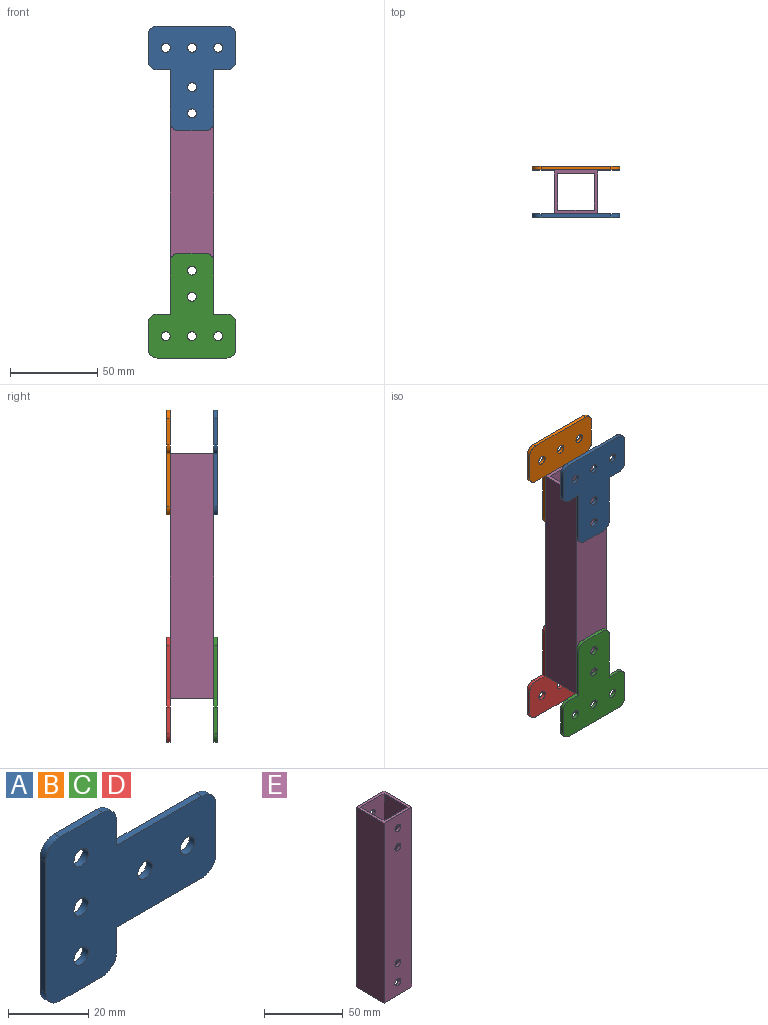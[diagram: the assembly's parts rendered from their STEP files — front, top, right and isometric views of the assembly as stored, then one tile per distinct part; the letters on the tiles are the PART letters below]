
ASSEMBLY  parts=5 mates=4
PART A: 21 faces, bbox 60x2x50 mm
  f0: plane 7.5x2mm, normal (1,0,0), area 15mm2, adj f12,f13,f14,f15
  f1: plane 15x2mm, normal (0,0,1), area 30mm2, adj f13,f14,f15,f16
  f2: plane 40x2mm, normal (-1,0,0), area 80mm2, adj f13,f14,f16,f17
  f3: plane 15x2mm, normal (0,0,-1), area 30mm2, adj f13,f14,f17,f18
  f4: plane 7.5x2mm, normal (1,0,0), area 15mm2, adj f5,f13,f14,f18
  f5: plane 30x2mm, normal (0,0,-1), area 60mm2, adj f4,f13,f14,f19
  f6: plane 15x2mm, normal (1,0,0), area 30mm2, adj f13,f14,f19,f20
  f7: cylinder r=2.55mm len=5.1mm, axis (0,1,0), area 32mm2, adj f13,f14
  f8: cylinder r=2.55mm len=5.1mm, axis (0,1,0), area 32mm2, adj f13,f14
  f9: cylinder r=2.55mm len=5.1mm, axis (0,1,0), area 32mm2, adj f13,f14
  f10: cylinder r=2.55mm len=5.1mm, axis (0,1,0), area 32mm2, adj f13,f14
  f11: cylinder r=2.55mm len=5.1mm, axis (0,1,0), area 32mm2, adj f13,f14
  f12: plane 30x2mm, normal (0,0,1), area 60mm2, adj f0,f13,f14,f20
  f13: plane 60x50mm, normal (0,-1,0), area 1990.7mm2, adj f0,f1,f2,f3,f4,f5,f6,f7
  f14: plane 60x50mm, normal (0,1,0), area 1990.7mm2, adj f0,f1,f2,f3,f4,f5,f6,f7
  f15: cylinder r=5mm len=5mm, axis (0,1,0), area 15.7mm2, adj f0,f1,f13,f14
  f16: cylinder r=5mm len=5mm, axis (0,1,0), area 15.7mm2, adj f1,f2,f13,f14
  f17: cylinder r=5mm len=5mm, axis (0,1,0), area 15.7mm2, adj f2,f3,f13,f14
  f18: cylinder r=5mm len=5mm, axis (0,1,0), area 15.7mm2, adj f3,f4,f13,f14
  f19: cylinder r=5mm len=5mm, axis (0,1,0), area 15.7mm2, adj f5,f6,f13,f14
  f20: cylinder r=5mm len=5mm, axis (0,1,0), area 15.7mm2, adj f6,f12,f13,f14
PART B: same geometry as A
PART C: same geometry as A
PART D: same geometry as A
PART E: 18 faces, bbox 25x25x140 mm
  f0: plane 140x21mm, normal (-1,0,0), area 2940mm2, adj f1,f7,f8,f9
  f1: plane 140x21mm, normal (0,1,0), area 2851.8mm2, adj f0,f2,f8,f9,f14,f15,f16,f17
  f2: plane 140x21mm, normal (1,0,0), area 2940mm2, adj f1,f7,f8,f9
  f3: plane 140x25mm, normal (-1,0,0), area 3500mm2, adj f4,f6,f8,f9
  f4: plane 140x25mm, normal (0,-1,0), area 3411.8mm2, adj f3,f5,f8,f9,f14,f15,f16,f17
  f5: plane 140x25mm, normal (1,0,0), area 3500mm2, adj f4,f6,f8,f9
  f6: plane 140x25mm, normal (0,1,0), area 3411.8mm2, adj f3,f5,f8,f9,f10,f11,f12,f13
  f7: plane 140x21mm, normal (0,-1,0), area 2851.8mm2, adj f0,f2,f8,f9,f10,f11,f12,f13
  f8: plane 25x25mm, normal (0,0,1), area 184mm2, adj f0,f1,f2,f3,f4,f5,f6,f7
  f9: plane 25x25mm, normal (0,0,-1), area 184mm2, adj f0,f1,f2,f3,f4,f5,f6,f7
  f10: cylinder r=2.65mm len=5.3mm, axis (0,-1,0), area 33.3mm2, adj f6,f7
  f11: cylinder r=2.65mm len=5.3mm, axis (0,-1,0), area 33.3mm2, adj f6,f7
  f12: cylinder r=2.65mm len=5.3mm, axis (0,-1,0), area 33.3mm2, adj f6,f7
  f13: cylinder r=2.65mm len=5.3mm, axis (0,-1,0), area 33.3mm2, adj f6,f7
  f14: cylinder r=2.65mm len=5.3mm, axis (0,-1,0), area 33.3mm2, adj f1,f4
  f15: cylinder r=2.65mm len=5.3mm, axis (0,-1,0), area 33.3mm2, adj f1,f4
  f16: cylinder r=2.65mm len=5.3mm, axis (0,-1,0), area 33.3mm2, adj f1,f4
  f17: cylinder r=2.65mm len=5.3mm, axis (0,-1,0), area 33.3mm2, adj f1,f4
PLACE A rot(axis=(0,1,0),90deg) t=(-37.79,-5.41,200.79)mm
PLACE B rot(axis=(0,1,0),90deg) t=(-37.79,21.59,200.79)mm
PLACE C rot(axis=(0,-1,0),90deg) t=(-37.79,-5.41,60.79)mm
PLACE D rot(axis=(0,-1,0),90deg) t=(-37.79,21.59,60.79)mm
PLACE E rot(axis=(0,1,0),0deg) t=(-37.79,7.09,60.79)mm
MATE planar A.f13 <-> C.f13  axis (0,-1,0) through (-37.79,-7.41,200.97)mm
MATE slider C.f10 <-> E.f10  axis (0,-1,0) through (-37.79,-7.41,70.79)mm
MATE planar E.f4 <-> A.f14  axis (0,-1,0) through (-37.79,-5.41,130.79)mm
MATE slider A.f10 <-> E.f13  axis (0,-1,0) through (-37.79,-7.41,190.79)mm
